# Revit family: IS_iLifeA_T4620_BIM_GB
name_source: partatom
category: Plumbing Fixtures
units: mm (PartAtom-declared; Revit-internal decimal feet)

## family parameters
Always vertical = No
Cut with Voids When Loaded = No
OmniClass Number = 23.45.05.14.14
OmniClass Title = Sinks/Lavatories
Part Type = Normal
Room Calculation Point = No
Round Connector Dimension = Use Diameter
Shared = No
Work Plane-Based = No

## types (2) — shared parameters
Accessories = https://www.idealstandard.co.uk
AreaUnits = millimetres
AssetType = fixed
BIMObjectName = IS_IdealStandard_Vanityunits_i.lifeA_T4620
BIMobject category = Wash Basins
BIMobject category code = wash-basins
BIMobject main category = Sanitary
BIMobject main category code = sanitary
BarCode = 8014140491361
Brand = Ideal Standard
Brand url = http://www.idealstandard.co.uk
ConnectionType = Plumbing
CurrencyUnit = £
CurrentRevision = 1
Date of publishing = 07/10/2022
DurationUnit = years
Edition number = 1
ElementType = fixed
ExpectedLife = 99
GTIN code = https://8014140491361
Help = https://www.idealstandard.co.uk
IFC Classification = Sanitary Terminal
IfcExportAs = IfcSanitaryTerminalType
IfcExportType = WASHHANDBASIN
Installation instructions = https://www.idealstandard.co.uk
InstallationDate = n /a
InstallationInstructions = https://www.idealstandard.co.uk
LinearUnits = millimetres
MainColor = White
MaintenanceInformation = https://www.idealstandard.co.uk
Manufacturer = Ideal Standard
Manufacturer name = Ideal Standard
ManufacturerURL = https://www.idealstandard.co.uk
Masterformat 2014 Code = 22 40 00
Masterformat 2014 Description = Plumbing Fixtures
Material = Fireclay
Material main = Fireclay
NBS Reference Code = 45-35-70/384
NBS Reference Description = WC Pans
Name = Vanityunits_i.lifeA_T4620_IdealStandard
NettWeight = 23.1
NominalDepth = 462 mm
NominalHeight = 157 mm
NominalWidth = 840 mm
OmniClass Code = 23-31 19 00
OmniClass Description = Toilets
Product Guid = 9574ad83-7f60-43b5-9b24-1dac21072865
Product SKU = T4620
Product certification = https://www.idealstandard.co.uk
Product data url = https://bimobject.com
Product family = I.life A
Product group = Basin
Product name = IDEAL STANDARD I.LIFE A VANITY 84 CM WITH CENTER TAPHOLE, WITH OVERFLOW
Product url = https://www.idealstandard.co.uk
ProductInformation = https://www.idealstandard.co.uk
QR code = http://bimobject.com
Shape = sculptured
Size = 840 x 462 x 157 mm
Space = Internal
SpareParts = https://www.idealstandard.co.uk
Technical description = https://www.idealstandard.co.uk
UNSPSC Code = 301815
URL = https://www.idealstandard.co.uk
Uniclass 1.4 Code = L72121
Uniclass 1.4 Description = Vanity units
Uniclass 2.0 Code = Pr_40_30_76_94
Uniclass 2.0 Description = Vanity Units
Uniclass 2015 Code = Pr_40_20_76_94
Uniclass 2015 Name = Vanity units
Uniclass2015Code = Pr_40_20_76_94
Uniclass2015Title = Vanity units
Uniclass2015Version = v1.27
Uniformat II Code = D2010
Uniformat II Description = Plumbing Fixtures
Version = 1
VolumeUnits = liters
WRASURL = https://www.wrasapprovals.co.uk
WarrantyDescription = manufacturer warranty
WarrantyDurationUnit = years
WashHandBasinMounting = Over furniture
WashHandBasinType = Vanity wasbasin
Weight Net (Kg) = 23.1
Youtube clip = https://www.wrasapprovals.co.uk

## per-type parameters (varying)
| type | Color | Description | Features | Finish | Model | ModelNumber | ModelReference |
| T462001 - Ideal Standard i.life A vanity 84 cm with center taphole, with overflow, white | White | Vanity 84 cm with center taphole, with overflow, white | Vanity 84 cm with center taphole, with overflow, white | White | T462001 | T462001 | I.life A Vanity 84 cm with center taphole, with overflow, white |
| T4620MA - Ideal Standard i.life A vanity 84 cm with center taphole, with overflow, white Ideal Plus | White Ideal Plus | Vanity 84 cm with center taphole, with overflow, white Ideal Plus | Vanity 84 cm with center taphole, with overflow, white Ideal Plus | White Ideal Plus | T4620MA | T4620MA | I.life A Vanity 84 cm with center taphole, with overflow, white Ideal Plus |

## geometry (parser evidence)
native form markers: Sweep x2
no freeform markers — native parametric forms only
